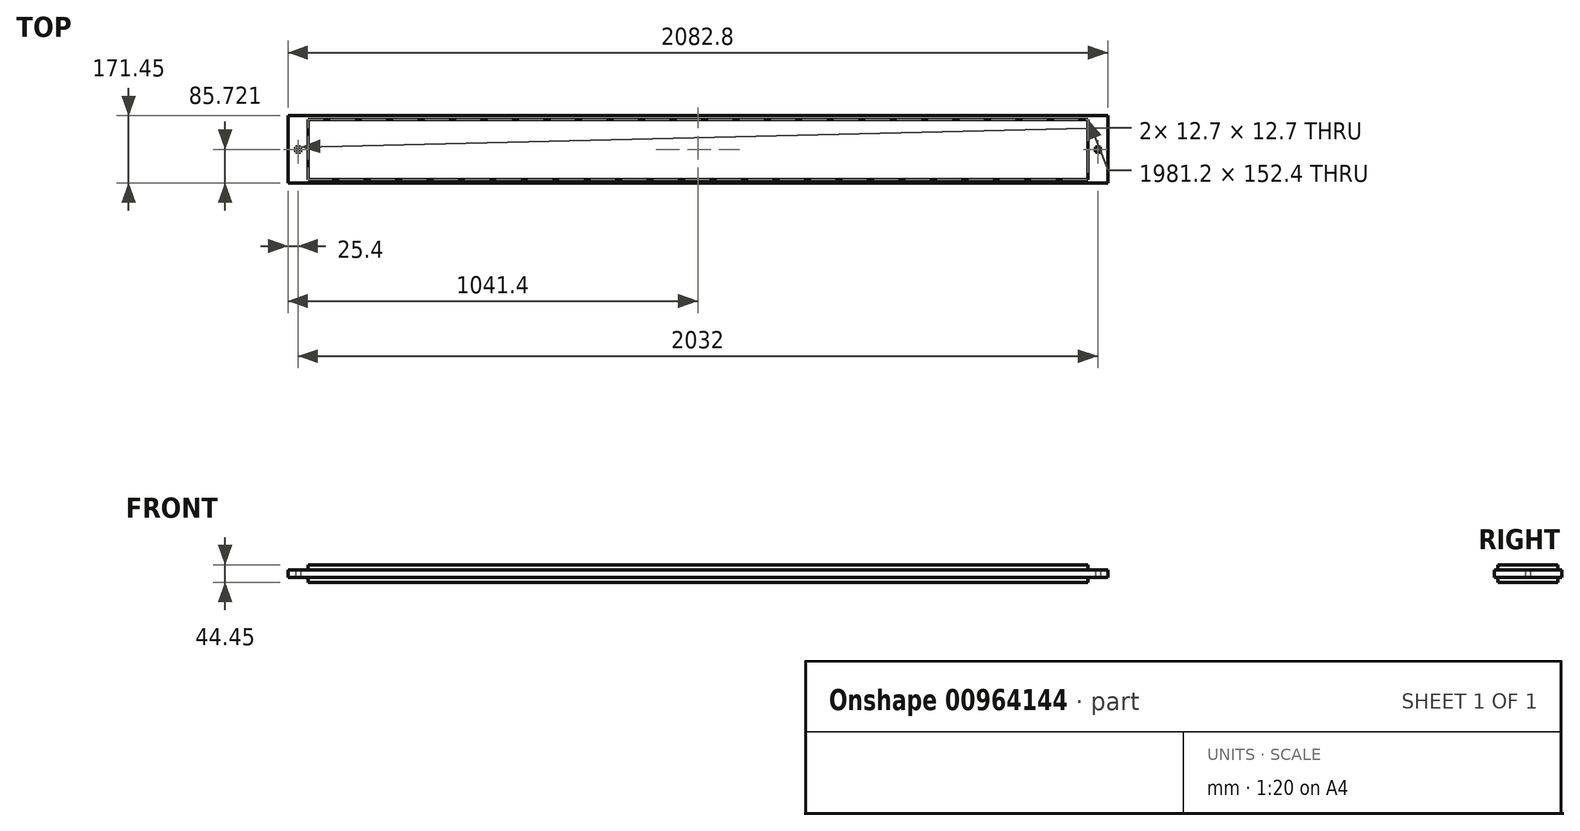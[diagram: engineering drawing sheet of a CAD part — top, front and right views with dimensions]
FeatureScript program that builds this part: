
annotation { "Feature Type Name" : "Feature", "Feature Type Description" : "" }
export const myFeature = defineFeature(function(context is Context, id is Id, definition is map)
    precondition{}
    {
        {
            var Q0;
            Q0=qCreatedBy(makeId("Top.planeOp"),FACE);
            var sketch = newSketch(context, id + "F0", { "sketchPlane" : qUnion([Q0])});
            skLineSegment(sketch, "E0.bottom", {"start": v(-960.45, -421.36) * mm, "end": v(1122.35, -421.36) * mm});
            skLineSegment(sketch, "E0.top", {"start": v(-960.45, -592.81) * mm, "end": v(1122.35, -592.81) * mm});
            skLineSegment(sketch, "E0.left", {"start": v(-960.45, -421.36) * mm, "end": v(-960.45, -592.81) * mm});
            skLineSegment(sketch, "E0.right", {"start": v(1122.35, -421.36) * mm, "end": v(1122.35, -592.81) * mm});
            skSolve(sketch);
        }
        {
            var Q0;
            Q0=qSketchRegion(id+"F0",true);
            extrude(context, id + "F1", {"entities" : qUnion([Q0]), "depth" : 44.45 * mm, "offsetDistance" : 25.4 * mm});
        }
        {
            var Q0;
            Q0=makeQuery(id+"F1.opExtrude","CAP_FACE",FACE,{"disambiguationData":[OSD([sQuery(id+"F0.wireOp",EDGE,"E0.bottom"),sQuery(id+"F0.wireOp",EDGE,"E0.top"),sQuery(id+"F0.wireOp",EDGE,"E0.left"),sQuery(id+"F0.wireOp",EDGE,"E0.right")])],"isStart":true});
            var sketch = newSketch(context, id + "F2", { "sketchPlane" : qUnion([Q0])});
            skLineSegment(sketch, "E1.bottom", {"start": v(-960.45, 421.36) * mm, "end": v(-909.65, 421.36) * mm});
            skLineSegment(sketch, "E1.top", {"start": v(-960.45, 592.81) * mm, "end": v(-909.65, 592.81) * mm});
            skLineSegment(sketch, "E1.left", {"start": v(-960.45, 592.81) * mm, "end": v(-960.45, 421.36) * mm});
            skLineSegment(sketch, "E1.right", {"start": v(-909.65, 592.81) * mm, "end": v(-909.65, 421.36) * mm});
            skLineSegment(sketch, "E2.bottom", {"start": v(1071.55, 421.36) * mm, "end": v(1122.35, 421.36) * mm});
            skLineSegment(sketch, "E2.top", {"start": v(1071.55, 592.81) * mm, "end": v(1122.35, 592.81) * mm});
            skLineSegment(sketch, "E2.left", {"start": v(1122.35, 592.81) * mm, "end": v(1122.35, 421.36) * mm});
            skLineSegment(sketch, "E2.right", {"start": v(1071.55, 592.81) * mm, "end": v(1071.55, 421.36) * mm});
            skLineSegment(sketch, "E3.bottom", {"start": v(-909.65, 592.81) * mm, "end": v(1071.55, 592.81) * mm});
            skLineSegment(sketch, "E3.top", {"start": v(-909.65, 583.29) * mm, "end": v(1071.55, 583.29) * mm});
            skLineSegment(sketch, "E3.left", {"start": v(-909.65, 592.81) * mm, "end": v(-909.65, 583.29) * mm});
            skLineSegment(sketch, "E3.right", {"start": v(1071.55, 592.81) * mm, "end": v(1071.55, 583.29) * mm});
            skLineSegment(sketch, "E4.bottom", {"start": v(-909.65, 421.36) * mm, "end": v(1071.55, 421.36) * mm});
            skLineSegment(sketch, "E4.top", {"start": v(-909.65, 430.89) * mm, "end": v(1071.55, 430.89) * mm});
            skLineSegment(sketch, "E4.left", {"start": v(-909.65, 421.36) * mm, "end": v(-909.65, 430.89) * mm});
            skLineSegment(sketch, "E4.right", {"start": v(1071.55, 421.36) * mm, "end": v(1071.55, 430.89) * mm});
            skSolve(sketch);
        }
        {
            var Q0;
            Q0=qSketchRegion(id+"F2",true);
            extrude(context, id + "F3", {"entities" : qUnion([Q0]), "operationType" : NewBodyOperationType.REMOVE, "oppositeDirection" : true, "depth" : 12.7 * mm, "offsetDistance" : 25.4 * mm});
        }
        {
            var Q0;
            Q0=makeQuery(id+"F1.opExtrude","CAP_FACE",FACE,{"disambiguationData":[OSD([sQuery(id+"F0.wireOp",EDGE,"E0.bottom"),sQuery(id+"F0.wireOp",EDGE,"E0.top"),sQuery(id+"F0.wireOp",EDGE,"E0.left"),sQuery(id+"F0.wireOp",EDGE,"E0.right"),sQuery(id+"F0.wireOp",EDGE,"qQXgVNNZ-AGSI-mXlc-8jnI-TWDtoKx84tdi.bottom"),sQuery(id+"F0.wireOp",EDGE,"qQXgVNNZ-AGSI-mXlc-8jnI-TWDtoKx84tdi.top"),sQuery(id+"F0.wireOp",EDGE,"qQXgVNNZ-AGSI-mXlc-8jnI-TWDtoKx84tdi.right"),sQuery(id+"F0.wireOp",EDGE,"eITyjntY-zXV5-UdZx-rjJQ-oeJIxLVityGO.bottom"),sQuery(id+"F0.wireOp",EDGE,"eITyjntY-zXV5-UdZx-rjJQ-oeJIxLVityGO.top"),sQuery(id+"F0.wireOp",EDGE,"eITyjntY-zXV5-UdZx-rjJQ-oeJIxLVityGO.right")])],"isStart":false});
            var sketch = newSketch(context, id + "F4", { "sketchPlane" : qUnion([Q0])});
            skLineSegment(sketch, "E5.bottom", {"start": v(-960.45, -421.36) * mm, "end": v(-960.45, -421.36) * mm});
            skLineSegment(sketch, "E6.bottom", {"start": v(1071.55, -421.36) * mm, "end": v(1122.35, -421.36) * mm});
            skLineSegment(sketch, "E6.top", {"start": v(1071.55, -592.81) * mm, "end": v(1122.35, -592.81) * mm});
            skLineSegment(sketch, "E6.left", {"start": v(1071.55, -421.36) * mm, "end": v(1071.55, -592.81) * mm});
            skLineSegment(sketch, "E6.right", {"start": v(1122.35, -421.36) * mm, "end": v(1122.35, -592.81) * mm});
            skLineSegment(sketch, "E7.bottom", {"start": v(-960.45, -592.81) * mm, "end": v(-909.65, -592.81) * mm});
            skLineSegment(sketch, "E7.top", {"start": v(-960.45, -421.36) * mm, "end": v(-909.65, -421.36) * mm});
            skLineSegment(sketch, "E7.left", {"start": v(-960.45, -592.81) * mm, "end": v(-960.45, -421.36) * mm});
            skLineSegment(sketch, "E7.right", {"start": v(-909.65, -592.81) * mm, "end": v(-909.65, -421.36) * mm});
            skLineSegment(sketch, "E8.bottom", {"start": v(-909.65, -592.81) * mm, "end": v(1071.55, -592.81) * mm});
            skLineSegment(sketch, "E8.top", {"start": v(-909.65, -583.29) * mm, "end": v(1071.55, -583.29) * mm});
            skLineSegment(sketch, "E8.left", {"start": v(-909.65, -592.81) * mm, "end": v(-909.65, -583.29) * mm});
            skLineSegment(sketch, "E8.right", {"start": v(1071.55, -592.81) * mm, "end": v(1071.55, -583.29) * mm});
            skLineSegment(sketch, "E9.bottom", {"start": v(-909.65, -421.36) * mm, "end": v(1071.55, -421.36) * mm});
            skLineSegment(sketch, "E9.top", {"start": v(-909.65, -430.89) * mm, "end": v(1071.55, -430.89) * mm});
            skLineSegment(sketch, "E9.left", {"start": v(-909.65, -421.36) * mm, "end": v(-909.65, -430.89) * mm});
            skLineSegment(sketch, "E9.right", {"start": v(1071.55, -421.36) * mm, "end": v(1071.55, -430.89) * mm});
            skSolve(sketch);
        }
        {
            var Q0;
            Q0=qSketchRegion(id+"F4",true);
            extrude(context, id + "F5", {"entities" : qUnion([Q0]), "operationType" : NewBodyOperationType.REMOVE, "oppositeDirection" : true, "depth" : 12.7 * mm, "offsetDistance" : 25.4 * mm});
        }
        {
            var Q0;
            Q0=makeQuery(id+"F3.boolean.opBoolean","COPY",FACE,{"derivedFrom":makeQuery(id+"F3.opExtrude","CAP_FACE",FACE,{"disambiguationData":[OSD([sQuery(id+"F2.wireOp",EDGE,"E2.bottom"),sQuery(id+"F2.wireOp",EDGE,"E2.top"),sQuery(id+"F2.wireOp",EDGE,"E2.left"),sQuery(id+"F2.wireOp",EDGE,"E2.right")])],"isStart":false})});
            var sketch = newSketch(context, id + "F6", { "sketchPlane" : qUnion([Q0])});
            skLineSegment(sketch, "E10.bottom", {"start": v(-941.4, 500.74) * mm, "end": v(-928.7, 500.74) * mm});
            skLineSegment(sketch, "E10.top", {"start": v(-941.4, 513.44) * mm, "end": v(-928.7, 513.44) * mm});
            skLineSegment(sketch, "E10.left", {"start": v(-941.4, 500.74) * mm, "end": v(-941.4, 513.44) * mm});
            skLineSegment(sketch, "E10.right", {"start": v(-928.7, 500.74) * mm, "end": v(-928.7, 513.44) * mm});
            skLineSegment(sketch, "E11.bottom", {"start": v(1090.6, 500.74) * mm, "end": v(1103.3, 500.74) * mm});
            skLineSegment(sketch, "E11.top", {"start": v(1090.6, 513.44) * mm, "end": v(1103.3, 513.44) * mm});
            skLineSegment(sketch, "E11.left", {"start": v(1090.6, 500.74) * mm, "end": v(1090.6, 513.44) * mm});
            skLineSegment(sketch, "E11.right", {"start": v(1103.3, 500.74) * mm, "end": v(1103.3, 513.44) * mm});
            skSolve(sketch);
        }
        {
            var Q0;
            Q0=qSketchRegion(id+"F6",true);
            extrude(context, id + "F7", {"entities" : qUnion([Q0]), "operationType" : NewBodyOperationType.REMOVE, "endBound" : BoundingType.THROUGH_ALL, "oppositeDirection" : true, "depth" : 25.4 * mm, "offsetDistance" : 25.4 * mm});
        }
    });
